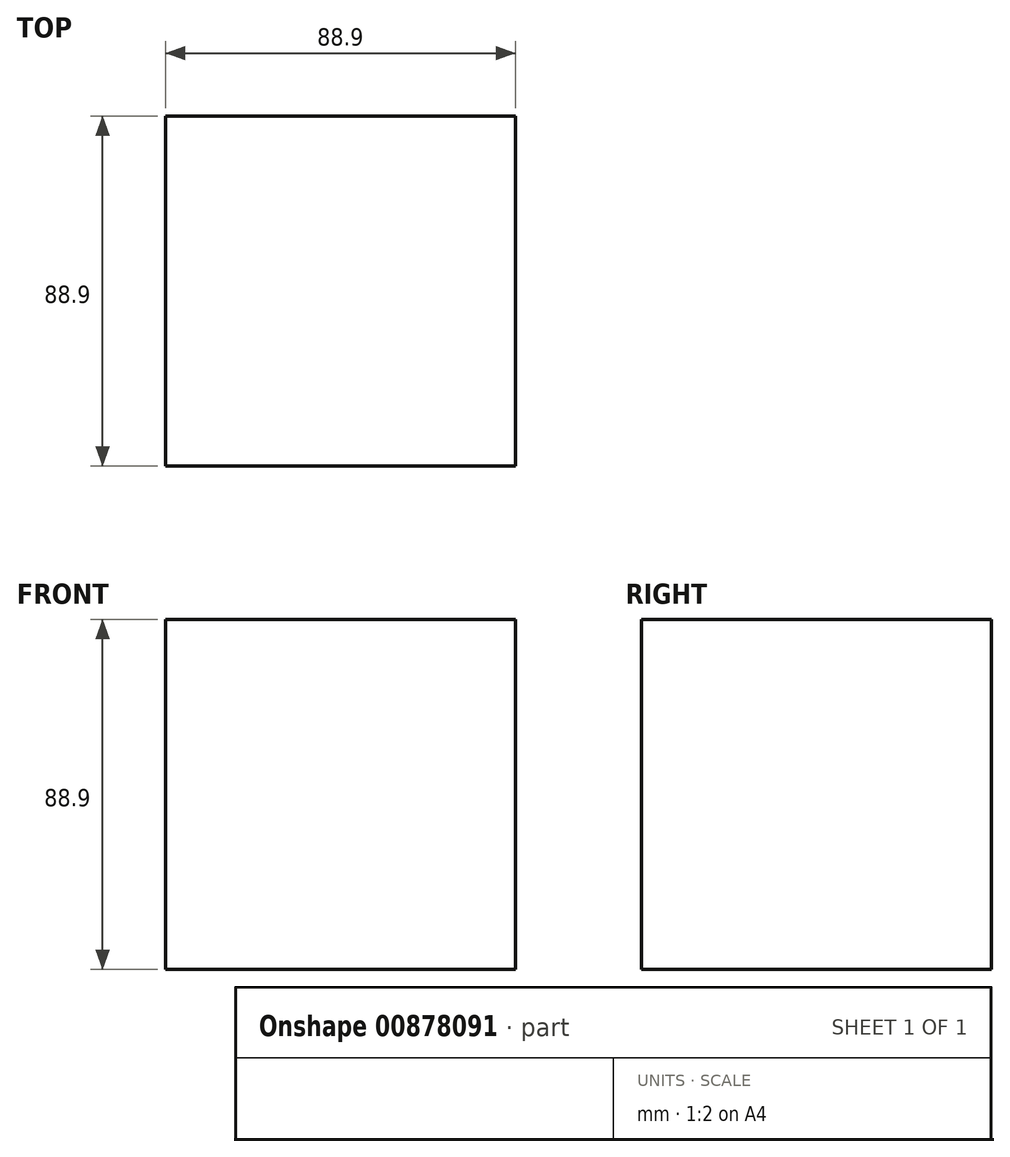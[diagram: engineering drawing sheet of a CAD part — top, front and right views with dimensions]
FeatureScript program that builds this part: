
annotation { "Feature Type Name" : "Feature", "Feature Type Description" : "" }
export const myFeature = defineFeature(function(context is Context, id is Id, definition is map)
    precondition{}
    {
        {
            var Q0;
            Q0=qCreatedBy(makeId("Top.planeOp"),FACE);
            var sketch = newSketch(context, id + "F0", { "sketchPlane" : qUnion([Q0])});
            skLineSegment(sketch, "E0.bottom", {"start": v(44.45, 44.45) * mm, "end": v(-44.45, 44.45) * mm});
            skLineSegment(sketch, "E0.top", {"start": v(44.45, -44.45) * mm, "end": v(-44.45, -44.45) * mm});
            skLineSegment(sketch, "E0.left", {"start": v(44.45, 44.45) * mm, "end": v(44.45, -44.45) * mm});
            skLineSegment(sketch, "E0.right", {"start": v(-44.45, 44.45) * mm, "end": v(-44.45, -44.45) * mm});
            skPoint(sketch, "E0.middle", {"position": v(0, 0) * mm});
            skSolve(sketch);
        }
        {
            var Q0;
            Q0=makeQuery(id+"F0.imprint","IMPRINT",FACE,{"disambiguationData":[TD([[makeQuery(id+"F0.imprint","IMPRINT",EDGE,{"derivedFrom":sQuery(id+"F0.wireOp",EDGE,"E0.bottom")}),1.0]])]});
            extrude(context, id + "F1", {"entities" : qUnion([Q0]), "endBound" : BoundingType.SYMMETRIC, "depth" : 88.9 * mm, "offsetDistance" : 25.4 * mm});
        }
    });
